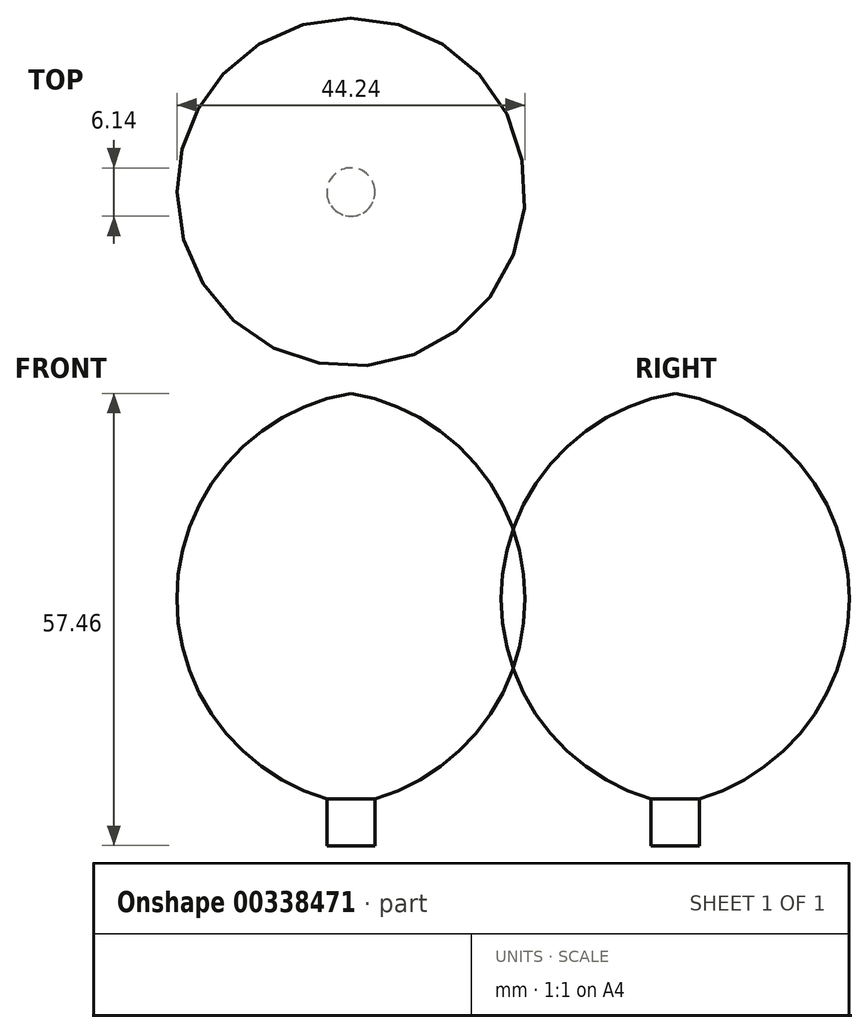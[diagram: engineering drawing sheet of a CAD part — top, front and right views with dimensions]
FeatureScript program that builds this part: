
annotation { "Feature Type Name" : "Feature", "Feature Type Description" : "" }
export const myFeature = defineFeature(function(context is Context, id is Id, definition is map)
    precondition{}
    {
        {
            var Q0;
            Q0=qCreatedBy(makeId("Front.planeOp"),FACE);
            var sketch = newSketch(context, id + "F0", { "sketchPlane" : qUnion([Q0])});
            skLineSegment(sketch, "E0", {"start": v(0, -30.31) * mm, "end": v(3.07, -30.31) * mm});
            skLineSegment(sketch, "E1", {"start": v(3.07, -30.31) * mm, "end": v(3.07, -24.37) * mm});
            skLineSegment(sketch, "E2", {"start": v(0, 27.15) * mm, "end": v(0, -30.31) * mm, "construction": true});
            skLineSegment(sketch, "E3", {"start": v(0, 27.15) * mm, "end": v(0, -30.31) * mm});
            skArc(sketch, "E4", {"start": v(3.07, -24.37) * mm, "mid": v(22.07, 2.62) * mm, "end": v(0, 27.15) * mm});
            skSolve(sketch);
        }
        {
            var Q0;
            Q0=makeQuery(id+"F0.imprint","IMPRINT",FACE,{"disambiguationData":[TD([[makeQuery(id+"F0.imprint","IMPRINT",EDGE,{"derivedFrom":sQuery(id+"F0.wireOp",EDGE,"E0")}),1.0]])]});
            var Q1;
            Q1=sQuery(id+"F0.wireOp",EDGE,"E3");
            revolve(context, id + "F1", {"entities" : qUnion([Q0]), "axis" : qUnion([Q1]), "revolveType" : RevolveType.FULL});
        }
    });
